# Revit family: HerzCon-узел прямого подключения для фанкойлов 90мм
name_source: partatom
category: Rohrzubehör
revit_build: Autodesk Revit 2018 (Build: 20190510_1515(x64)
units: mm (PartAtom-declared; Revit-internal decimal feet)

## family parameters
Arbeitsebenenbasiert = Nein
Beim Laden mit Abzugskörper schneiden = Nein
Bemaßung runder Anschluss = Durchmesser verwenden
Gemeinsam genutzt = Nein
Immer vertikal = Ja
OmniClass-Nummer = 23.65.55.14
OmniClass-Titel = Valves for Liquid Services
Teiletyp = Unterbricht

## types (1)
- DN25
    D01 = 15 mm  [stored 0.0492126 ft]
    D02 = 27 mm  [stored 0.0885827 ft]
    D03 = 21.25 mm  [stored 0.0697178 ft]
    D04 = 15.5 mm  [stored 0.050853 ft]
    D05 = 33.8 mm  [stored 0.110892 ft]
    D06 = 32.6 mm  [stored 0.106955 ft]
    D07 = 14.85 mm  [stored 0.0487205 ft]
    D08 = 19.1 mm  [stored 0.062664 ft]
    D09 = 18.9 mm  [stored 0.0620079 ft]
    D10 = 13 mm
    D11 = 20 mm  [stored 0.0656168 ft]
    H01 = 39.5 mm
    H02 = 28 mm  [stored 0.0918635 ft]
    Hersteller = HERZ Armaturen Ges.m.b.H.
    L01 = 19.85 mm  [stored 0.0651247 ft]
    L02 = 4.8 mm  [stored 0.015748 ft]
    L03 = 18 mm  [stored 0.0590551 ft]
    L04 = 45 mm  [stored 0.147638 ft]
    L05 = 22 mm  [stored 0.0721785 ft]
    L06 = 20.5 mm  [stored 0.0672572 ft]
    L07 = 12.5 mm  [stored 0.0410105 ft]
    L08 = 14.75 mm
    L09 = 16 mm  [stored 0.0524934 ft]
    L10 = 25 mm  [stored 0.082021 ft]
    L11 = 14 mm  [stored 0.0459318 ft]
    SCRNCODE = 05;04;04
    SCRNSEQ = ARM;TYP_ARM="DURR";02
    URL = www.herz-armaturen.ru
    kvs-Wert (обычная работа) = 2.75
    kvs-Wert (работа байпаса) = 10.00
    Корпус = латунь, устойчивая к селективной цинковой коррозии
    Макс. дифференциальное давление = 400000.0 Pa
    Макс. рабочая температура = 130 °C
    Макс. рабочее давление = 2500000.0 Pa
    Мембрана и уплотнительное кольцо O-Ring = EPDM
    Мин. рабочая температура = -20 °C
    Применение = HerzCON был разработан для простого подключения фанкойлов или AHU.
HerzCON - это устройство, состоящее из независимого от давления комби-клапана - регулятора расхода (4006), HERZ фильтра-грязевика, HERZ крана для слива (2512) и двух HERZ мультифункциональных шаровых кранов.
Включение, выключение и модульное управление возможно производить через приводы 0 - 10 В.
Приводы могут быть интегрированы в BMS при необходимости.
Устройство обеспечивает независимое от давления управление и в то же время гарантирует постоянный расход для конечного потребителя, максимизируя энергоэффективность системы.
Устройство HerzCON также позволяет производить промывку и запирание.
HerzCON предназначен для работы как в системах холодоснабжения, так и теплоснабжения.
Кран для слива, установленный на сетчатом фильтре, позволяет производить промывку устройства без необходимости извлечения сетчатого фильтра, а также позволяет очищать сетчатый фильтр в самом устройстве.
    Среда = Вода для системы отопления подготавливается в соответствии с ÖNORM H5195 или VDI 2035.
Возможно использование этилена или пропиленгликоля в концентрации 25-50% объема.
    Теплоизолирующий бокс = EPP, вспененный полипропилен, паронепроницаемый, антидиффузионный, черного цвета
    Ход = 4 мм

note: [stored X ft] marks values corroborated as IEEE doubles in the binary element streams (Revit-internal decimal feet)
